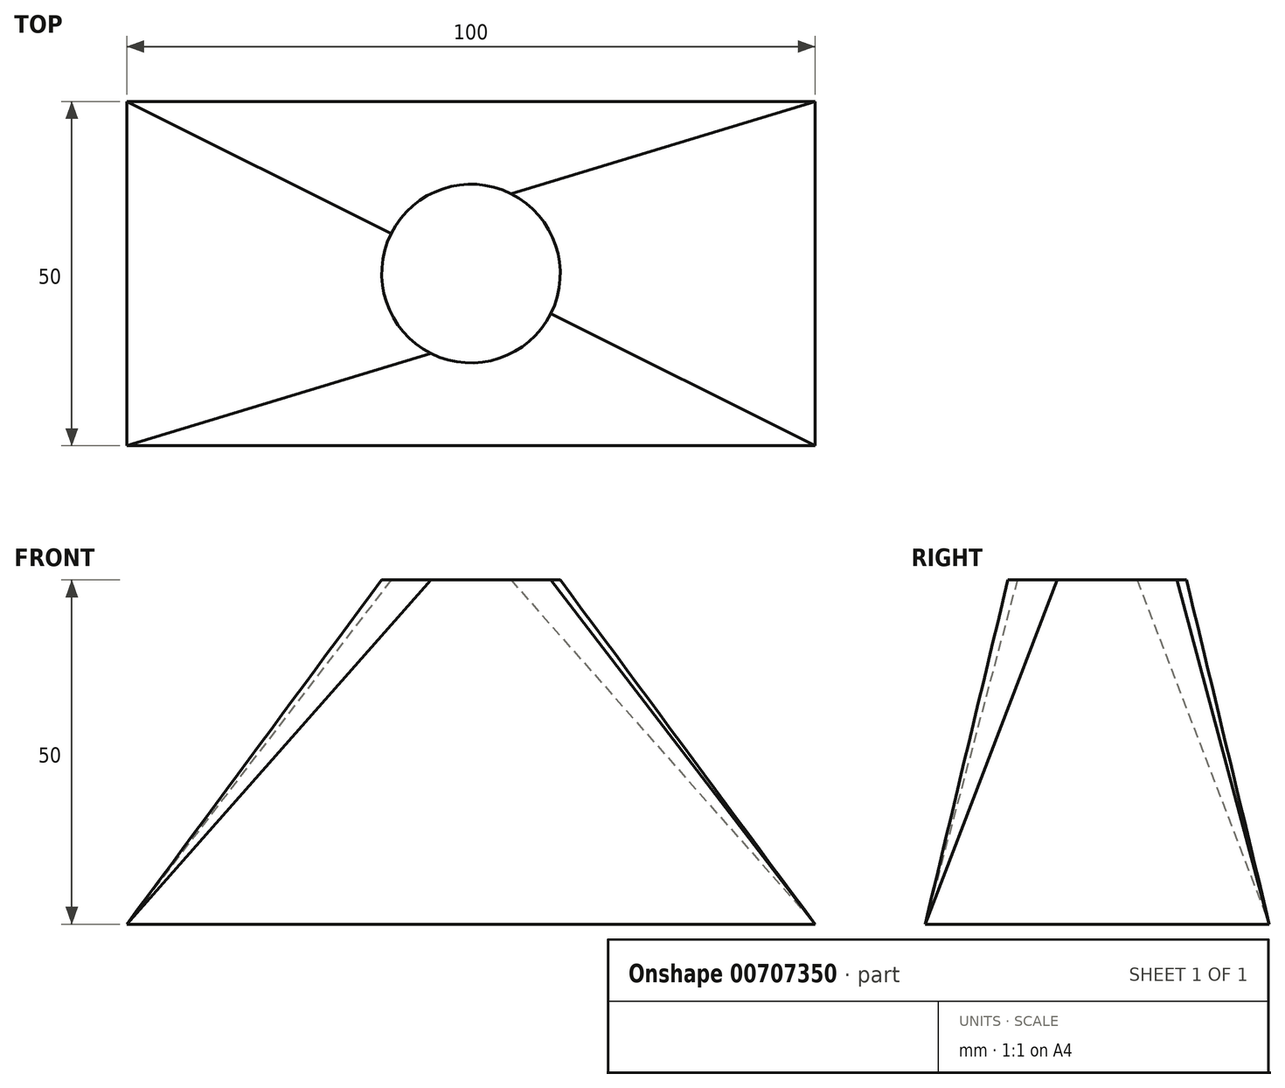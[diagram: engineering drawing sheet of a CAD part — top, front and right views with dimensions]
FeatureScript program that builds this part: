
annotation { "Feature Type Name" : "Feature", "Feature Type Description" : "" }
export const myFeature = defineFeature(function(context is Context, id is Id, definition is map)
    precondition{}
    {
        {
            var Q0;
            Q0=qCreatedBy(makeId("Top.planeOp"),FACE);
            var sketch = newSketch(context, id + "F0", { "sketchPlane" : qUnion([Q0])});
            skLineSegment(sketch, "E0.bottom", {"start": v(-50, 25) * mm, "end": v(50, 25) * mm});
            skLineSegment(sketch, "E0.top", {"start": v(-50, -25) * mm, "end": v(50, -25) * mm});
            skLineSegment(sketch, "E0.left", {"start": v(-50, 25) * mm, "end": v(-50, -25) * mm});
            skLineSegment(sketch, "E0.right", {"start": v(50, 25) * mm, "end": v(50, -25) * mm});
            skSolve(sketch);
        }
        {
            var Q0;
            Q0=qCreatedBy(makeId("Top.planeOp"),FACE);
            cPlane(context, id + "F1", {"entities" : qUnion([Q0]), "cplaneType" : CPlaneType.OFFSET, "offset" : 50 * mm, "width" : 150 * mm, "height" : 150 * mm});
        }
        {
            var Q0;
            Q0=qCreatedBy(id+"F1.planeOp",FACE);
            var sketch = newSketch(context, id + "F2", { "sketchPlane" : qUnion([Q0])});
            skCircle(sketch, "E1", {"center": v(0, 0) * mm, "radius": 12.97 * mm});
            skSolve(sketch);
        }
        {
            var Q0;
            Q0=makeQuery(id+"F2.imprint","IMPRINT",FACE,{"disambiguationData":[TD([[makeQuery(id+"F2.imprint","IMPRINT",EDGE,{"derivedFrom":sQuery(id+"F2.wireOp",EDGE,"E1")}),1.0]])]});
            var Q1;
            Q1=makeQuery(id+"F0.imprint","IMPRINT",FACE,{"disambiguationData":[TD([[makeQuery(id+"F0.imprint","IMPRINT",EDGE,{"derivedFrom":sQuery(id+"F0.wireOp",EDGE,"E0.bottom")}),-1.0]])]});
            loft(context, id + "F3", {"sheetProfilesArray" : [{ "sheetProfileEntities" : qUnion([Q0]) }, { "sheetProfileEntities" : qUnion([Q1]) }]});
        }
    });
